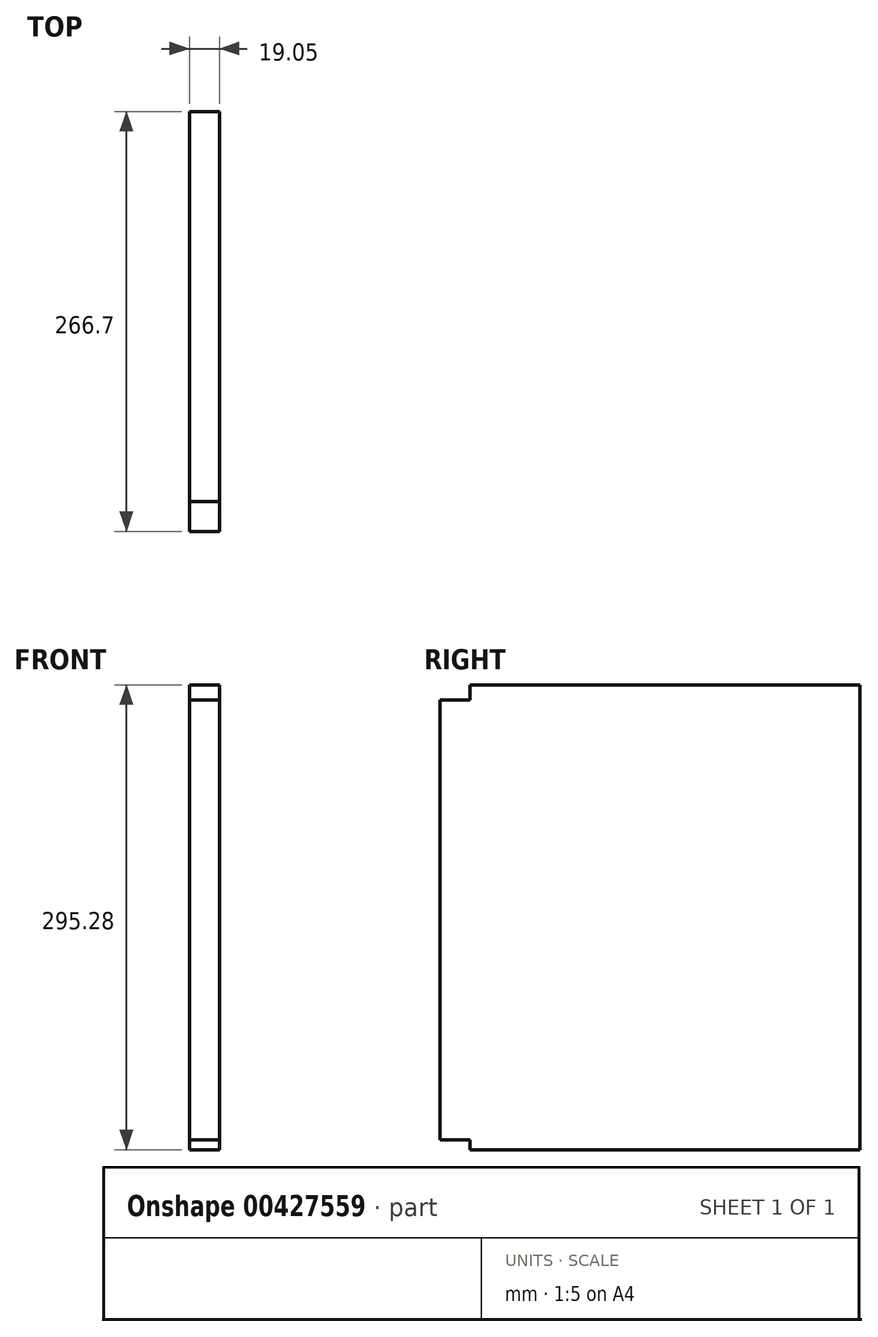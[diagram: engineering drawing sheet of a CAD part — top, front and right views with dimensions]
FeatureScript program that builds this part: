
annotation { "Feature Type Name" : "Feature", "Feature Type Description" : "" }
export const myFeature = defineFeature(function(context is Context, id is Id, definition is map)
    precondition{}
    {
        {
            var Q0;
            Q0=qCreatedBy(makeId("Front.planeOp"),FACE);
            var sketch = newSketch(context, id + "F0", { "sketchPlane" : qUnion([Q0])});
            skLineSegment(sketch, "E0.bottom", {"start": v(0, 0) * mm, "end": v(19.05, 0) * mm});
            skLineSegment(sketch, "E0.top", {"start": v(0, 295.28) * mm, "end": v(19.05, 295.28) * mm});
            skLineSegment(sketch, "E0.left", {"start": v(0, 0) * mm, "end": v(0, 295.28) * mm});
            skLineSegment(sketch, "E0.right", {"start": v(19.05, 0) * mm, "end": v(19.05, 295.28) * mm});
            skSolve(sketch);
        }
        {
            var Q0;
            Q0 = qSketchRegion(id + "F0", true);
            extrude(context, id + "F1", {"entities" : qUnion([Q0]), "depth" : 266.7 * mm});
        }
        {
            var Q0;
            Q0=makeQuery(id+"F1.opExtrude","SWEPT_FACE",FACE,{"disambiguationData":[OSD([sQuery(id+"F0.wireOp",EDGE,"E0.right")])]});
            var sketch = newSketch(context, id + "F2", { "sketchPlane" : qUnion([Q0])});
            skLineSegment(sketch, "E1.bottom", {"start": v(-266.7, 295.28) * mm, "end": v(-247.65, 295.28) * mm});
            skLineSegment(sketch, "E1.top", {"start": v(-266.7, 285.75) * mm, "end": v(-247.65, 285.75) * mm});
            skLineSegment(sketch, "E1.left", {"start": v(-266.7, 295.28) * mm, "end": v(-266.7, 285.75) * mm});
            skLineSegment(sketch, "E1.right", {"start": v(-247.65, 295.28) * mm, "end": v(-247.65, 285.75) * mm});
            skLineSegment(sketch, "E2.bottom", {"start": v(-266.7, 0) * mm, "end": v(-247.65, 0) * mm});
            skLineSegment(sketch, "E2.top", {"start": v(-266.7, 6.35) * mm, "end": v(-247.65, 6.35) * mm});
            skLineSegment(sketch, "E2.left", {"start": v(-266.7, 0) * mm, "end": v(-266.7, 6.35) * mm});
            skLineSegment(sketch, "E2.right", {"start": v(-247.65, 0) * mm, "end": v(-247.65, 6.35) * mm});
            skSolve(sketch);
        }
        {
            var Q0;
            Q0 = qSketchRegion(id + "F2", true);
            extrude(context, id + "F3", {"entities" : qUnion([Q0]), "operationType" : NewBodyOperationType.REMOVE, "oppositeDirection" : true, "depth" : 25.4 * mm});
        }
    });
